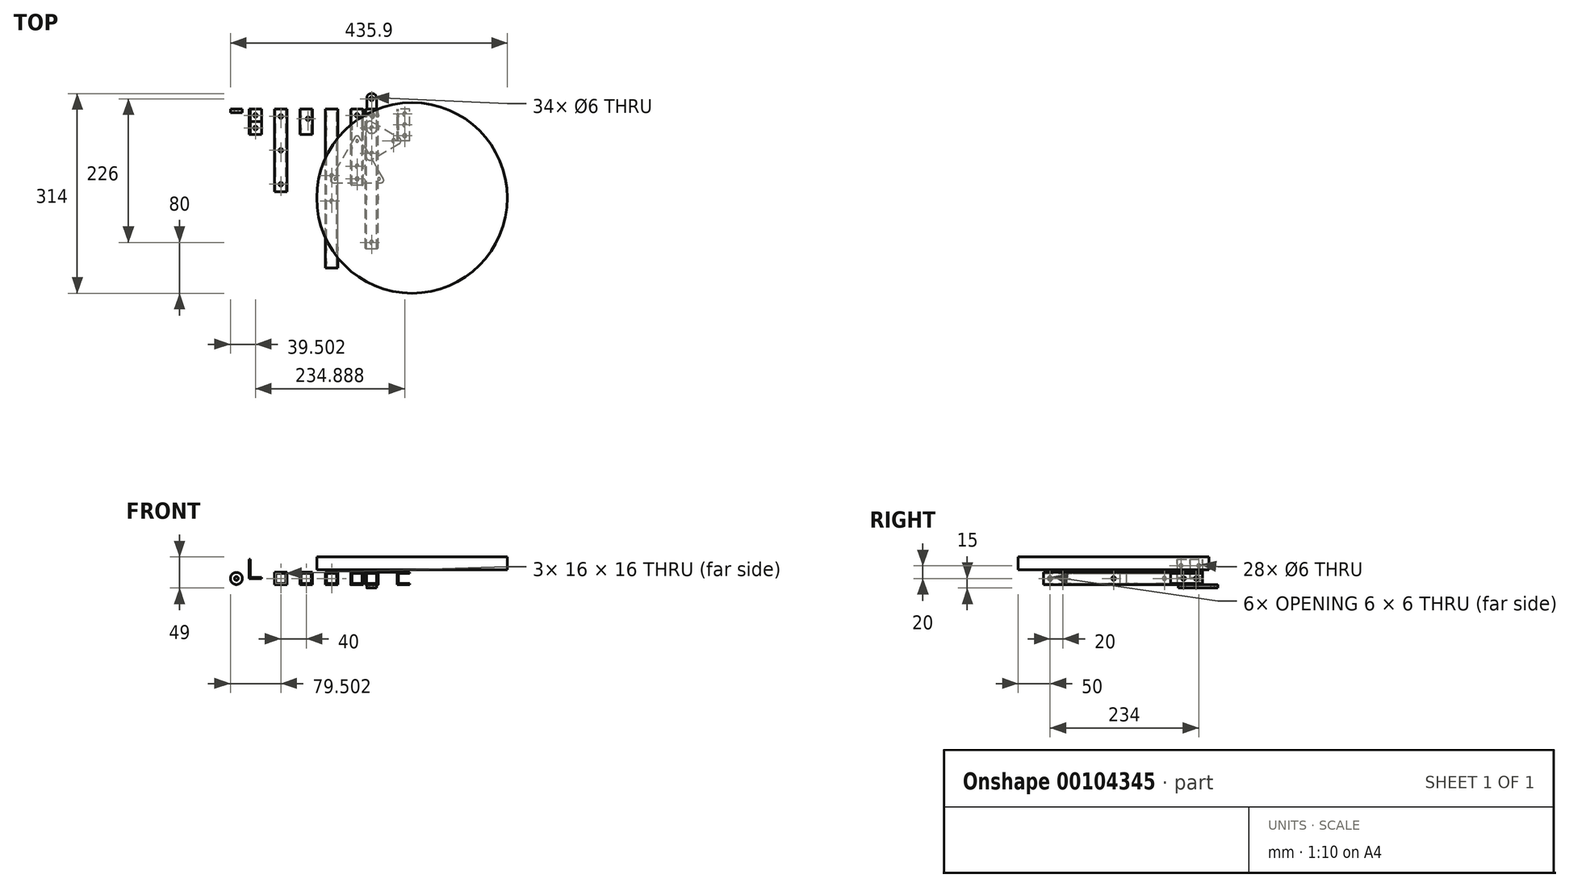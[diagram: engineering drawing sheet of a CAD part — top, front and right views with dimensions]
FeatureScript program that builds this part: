
annotation { "Feature Type Name" : "Feature", "Feature Type Description" : "" }
export const myFeature = defineFeature(function(context is Context, id is Id, definition is map)
    precondition{}
    {
        {
            var Q0;
            Q0=qCreatedBy(makeId("Front.planeOp"),FACE);
            var sketch = newSketch(context, id + "F0", { "sketchPlane" : qUnion([Q0])});
            skLineSegment(sketch, "E0.bottom", {"start": v(-10, 10) * mm, "end": v(10, 10) * mm});
            skLineSegment(sketch, "E0.top", {"start": v(-10, -10) * mm, "end": v(10, -10) * mm});
            skLineSegment(sketch, "E0.left", {"start": v(-10, 10) * mm, "end": v(-10, -10) * mm});
            skLineSegment(sketch, "E0.right", {"start": v(10, 10) * mm, "end": v(10, -10) * mm});
            skLineSegment(sketch, "E1.bottom", {"start": v(-8, 8) * mm, "end": v(8, 8) * mm});
            skLineSegment(sketch, "E1.top", {"start": v(-8, -8) * mm, "end": v(8, -8) * mm});
            skLineSegment(sketch, "E1.left", {"start": v(-8, 8) * mm, "end": v(-8, -8) * mm});
            skLineSegment(sketch, "E1.right", {"start": v(8, 8) * mm, "end": v(8, -8) * mm});
            skSolve(sketch);
        }
        {
            var Q0;
            Q0 = qSketchRegion(id + "F0", true);
            extrude(context, id + "F1", {"entities" : qUnion([Q0]), "offsetDistance" : 25 * mm, "depth" : 220 * mm});
        }
        {
            var Q0;
            Q0=makeQuery(id+"F1.opExtrude","SWEPT_FACE",FACE,{"disambiguationData":[OSD([sQuery(id+"F0.wireOp",EDGE,"E0.bottom")])]});
            var sketch = newSketch(context, id + "F2", { "sketchPlane" : qUnion([Q0])});
            skCircle(sketch, "E2", {"center": v(0, -30) * mm, "radius": 3 * mm});
            skCircle(sketch, "E3", {"center": v(0, -70) * mm, "radius": 3 * mm});
            skCircle(sketch, "E4", {"center": v(0, -210) * mm, "radius": 3 * mm});
            skSolve(sketch);
        }
        {
            var Q0;
            Q0 = qSketchRegion(id + "F2", true);
            var Q1;
            Q1=makeQuery(id+"F1.opExtrude","SWEPT_FACE",FACE,{"disambiguationData":[OSD([sQuery(id+"F0.wireOp",EDGE,"E0.top")])]});
            extrude(context, id + "F3", {"entities" : qUnion([Q0]), "operationType" : NewBodyOperationType.REMOVE, "endBound" : BoundingType.UP_TO_SURFACE, "oppositeDirection" : true, "endBoundEntityFace" : qUnion([Q1]), "offsetDistance" : 25 * mm, "depth" : 25 * mm});
        }
        {
            var Q0;
            Q0=makeQuery(id+"F1.opExtrude","SWEPT_FACE",FACE,{"disambiguationData":[OSD([sQuery(id+"F0.wireOp",EDGE,"E0.bottom")])]});
            var sketch = newSketch(context, id + "F4", { "sketchPlane" : qUnion([Q0])});
            skLineSegment(sketch, "E5", {"start": v(-8.66, -85) * mm, "end": v(-8.66, -15) * mm});
            skLineSegment(sketch, "E6", {"start": v(-8.66, -15) * mm, "end": v(51.96, -50) * mm});
            skLineSegment(sketch, "E7", {"start": v(51.96, -50) * mm, "end": v(-8.66, -85) * mm});
            skCircle(sketch, "E8", {"center": v(0, -30) * mm, "radius": 3 * mm});
            skLineSegment(sketch, "E9", {"start": v(-8.66, -50) * mm, "end": v(51.96, -50) * mm, "construction": true});
            skLineSegment(sketch, "E10", {"start": v(-8.66, -15) * mm, "end": v(21.65, -67.5) * mm, "construction": true});
            skCircle(sketch, "E11.1.0", {"center": v(0, -70) * mm, "radius": 3 * mm});
            skCircle(sketch, "E11.2.0", {"center": v(34.64, -50) * mm, "radius": 3 * mm});
            skPoint(sketch, "E11.center", {"position": v(11.55, -50) * mm});
            skSolve(sketch);
        }
        {
            var Q0;
            Q0 = qSketchRegion(id + "F4", true);
            extrude(context, id + "F5", {"entities" : qUnion([Q0]), "depth" : 2 * mm});
        }
        {
            var Q0;
            Q0=makeQuery(id+"F5.opExtrude","SWEPT_EDGE",EDGE,{"disambiguationData":[OSD([sQuery(id+"F4.wireOp",EDGE,"E5"),sQuery(id+"F4.wireOp",EDGE,"E7")])]});
            var Q1;
            Q1=makeQuery(id+"F5.opExtrude","SWEPT_EDGE",EDGE,{"disambiguationData":[OSD([sQuery(id+"F4.wireOp",EDGE,"E5"),sQuery(id+"F4.wireOp",EDGE,"E6")])]});
            var Q2;
            Q2=makeQuery(id+"F5.opExtrude","SWEPT_EDGE",EDGE,{"disambiguationData":[OSD([sQuery(id+"F4.wireOp",EDGE,"E6"),sQuery(id+"F4.wireOp",EDGE,"E7")])]});
            fillet(context, id + "F6", {"entities" : qUnion([Q0, Q1, Q2]), "radius" : 6 * mm, "tangentPropagation" : true, "allowEdgeOverflow" : false});
        }
        {
            var Q0;
            Q0=makeQuery(id+"F1.opExtrude","SWEPT_FACE",FACE,{"disambiguationData":[OSD([sQuery(id+"F0.wireOp",EDGE,"E0.top")])]});
            var sketch = newSketch(context, id + "F7", { "sketchPlane" : qUnion([Q0])});
            skCircle(sketch, "E12", {"center": v(0, 10) * mm, "radius": 3 * mm});
            skSolve(sketch);
        }
        {
            var Q0;
            Q0 = qSketchRegion(id + "F7", true);
            extrude(context, id + "F8", {"entities" : qUnion([Q0]), "operationType" : NewBodyOperationType.REMOVE, "endBound" : BoundingType.UP_TO_NEXT, "oppositeDirection" : true, "depth" : 25 * mm});
        }
        {
            var Q0;
            Q0=makeQuery(id+"F1.opExtrude","SWEPT_FACE",FACE,{"disambiguationData":[OSD([sQuery(id+"F0.wireOp",EDGE,"E0.bottom")])]});
            var sketch = newSketch(context, id + "F9", { "sketchPlane" : qUnion([Q0])});
            skCircle(sketch, "E13", {"center": v(0, -10) * mm, "radius": 5 * mm});
            skSolve(sketch);
        }
        {
            var Q0;
            Q0 = qSketchRegion(id + "F9", true);
            extrude(context, id + "F10", {"entities" : qUnion([Q0]), "operationType" : NewBodyOperationType.REMOVE, "endBound" : BoundingType.UP_TO_NEXT, "oppositeDirection" : true, "depth" : 25 * mm, "offsetDistance" : 25 * mm});
        }
        {
            var Q0;
            Q0=makeQuery(id+"F1.opExtrude","SWEPT_FACE",FACE,{"disambiguationData":[OSD([sQuery(id+"F0.wireOp",EDGE,"E0.top")])]});
            var sketch = newSketch(context, id + "F11", { "sketchPlane" : qUnion([Q0])});
            skLineSegment(sketch, "E14.bottom", {"start": v(7.5, 38) * mm, "end": v(-7.5, 38) * mm});
            skLineSegment(sketch, "E14.top", {"start": v(7.5, -24) * mm, "end": v(-7.5, -24) * mm});
            skLineSegment(sketch, "E14.left", {"start": v(7.5, 38) * mm, "end": v(7.5, -24) * mm});
            skLineSegment(sketch, "E14.right", {"start": v(-7.5, 38) * mm, "end": v(-7.5, -24) * mm});
            skCircle(sketch, "E15", {"center": v(0, 30) * mm, "radius": 3 * mm});
            skCircle(sketch, "E16", {"center": v(0, 10) * mm, "radius": 3 * mm});
            skCircle(sketch, "E17", {"center": v(0, -16) * mm, "radius": 3 * mm});
            skPoint(sketch, "E18", {"position": v(0, -24) * mm});
            skPoint(sketch, "E19", {"position": v(34.64, 50) * mm});
            skPoint(sketch, "E20", {"position": v(0, 210) * mm});
            skSolve(sketch);
        }
        {
            var Q0;
            Q0 = qSketchRegion(id + "F11", true);
            extrude(context, id + "F12", {"entities" : qUnion([Q0]), "depth" : 5 * mm});
        }
        {
            var Q0;
            Q0=qCreatedBy(makeId("Front.planeOp"),FACE);
            var sketch = newSketch(context, id + "F13", { "sketchPlane" : qUnion([Q0])});
            skLineSegment(sketch, "E21", {"start": v(60, 10) * mm, "end": v(40, 10) * mm});
            skLineSegment(sketch, "E22", {"start": v(40, 10) * mm, "end": v(40, -10) * mm});
            skLineSegment(sketch, "E23", {"start": v(40, -10) * mm, "end": v(60, -10) * mm});
            skLineSegment(sketch, "E24", {"start": v(60, -10) * mm, "end": v(60, -8) * mm});
            skLineSegment(sketch, "E25", {"start": v(60, -8) * mm, "end": v(42, -8) * mm});
            skLineSegment(sketch, "E26", {"start": v(42, -8) * mm, "end": v(42, 8) * mm});
            skLineSegment(sketch, "E27", {"start": v(42, 8) * mm, "end": v(60, 8) * mm});
            skLineSegment(sketch, "E28", {"start": v(60, 8) * mm, "end": v(60, 10) * mm});
            skLineSegment(sketch, "E29", {"start": v(42, 8) * mm, "end": v(40, 8) * mm, "construction": true});
            skSolve(sketch);
        }
        {
            var Q0;
            Q0 = qSketchRegion(id + "F13", true);
            extrude(context, id + "F14", {"entities" : qUnion([Q0]), "depth" : 50 * mm});
        }
        {
            var Q0;
            Q0=makeQuery(id+"F14.opExtrude","SWEPT_FACE",FACE,{"disambiguationData":[OSD([sQuery(id+"F13.wireOp",EDGE,"E23")])]});
            var sketch = newSketch(context, id + "F15", { "sketchPlane" : qUnion([Q0])});
            skCircle(sketch, "E30", {"center": v(52, 25) * mm, "radius": 3 * mm});
            skCircle(sketch, "E31", {"center": v(52, 8) * mm, "radius": 3 * mm});
            skSolve(sketch);
        }
        {
            var Q0;
            Q0 = qSketchRegion(id + "F15", true);
            extrude(context, id + "F16", {"entities" : qUnion([Q0]), "operationType" : NewBodyOperationType.REMOVE, "endBound" : BoundingType.UP_TO_NEXT, "oppositeDirection" : true, "depth" : 25 * mm});
        }
        {
            var Q0;
            Q0=makeQuery(id+"F14.opExtrude","SWEPT_FACE",FACE,{"disambiguationData":[OSD([sQuery(id+"F13.wireOp",EDGE,"E21")])]});
            var sketch = newSketch(context, id + "F17", { "sketchPlane" : qUnion([Q0])});
            skCircle(sketch, "E32", {"center": v(52, -42) * mm, "radius": 3 * mm});
            skPoint(sketch, "E33", {"position": v(52, -25) * mm});
            skSolve(sketch);
        }
        {
            var Q0;
            Q0 = qSketchRegion(id + "F17", true);
            var Q1;
            Q1=makeQuery(id+"F14.opExtrude","SWEPT_FACE",FACE,{"disambiguationData":[OSD([sQuery(id+"F13.wireOp",EDGE,"E23")])]});
            extrude(context, id + "F18", {"entities" : qUnion([Q0]), "operationType" : NewBodyOperationType.REMOVE, "endBound" : BoundingType.UP_TO_SURFACE, "oppositeDirection" : true, "endBoundEntityFace" : qUnion([Q1]), "offsetDistance" : 25 * mm, "depth" : 25 * mm});
        }
        {
            var Q0;
            Q0=makeQuery(id+"F12.opExtrude","SWEPT_EDGE",EDGE,{"disambiguationData":[OSD([sQuery(id+"F11.wireOp",EDGE,"E14.bottom"),sQuery(id+"F11.wireOp",EDGE,"E14.left")])]});
            var Q1;
            Q1=makeQuery(id+"F12.opExtrude","SWEPT_EDGE",EDGE,{"disambiguationData":[OSD([sQuery(id+"F11.wireOp",EDGE,"E14.bottom"),sQuery(id+"F11.wireOp",EDGE,"E14.right")])]});
            var Q2;
            Q2=makeQuery(id+"F12.opExtrude","SWEPT_EDGE",EDGE,{"disambiguationData":[OSD([sQuery(id+"F11.wireOp",EDGE,"E14.top"),sQuery(id+"F11.wireOp",EDGE,"E14.right")])]});
            var Q3;
            Q3=makeQuery(id+"F12.opExtrude","SWEPT_EDGE",EDGE,{"disambiguationData":[OSD([sQuery(id+"F11.wireOp",EDGE,"E14.top"),sQuery(id+"F11.wireOp",EDGE,"E14.left")])]});
            fillet(context, id + "F19", {"entities" : qUnion([Q0, Q1, Q2, Q3]), "radius" : 6 * mm, "tangentPropagation" : true, "allowEdgeOverflow" : false});
        }
        {
            var Q0;
            Q0=makeQuery(id+"F1.opExtrude","CAP_EDGE",EDGE,{"disambiguationData":[OSD([sQuery(id+"F0.wireOp",EDGE,"E0.right")])],"isStart":false});
            var Q1;
            Q1=makeQuery(id+"F1.opExtrude","CAP_EDGE",EDGE,{"disambiguationData":[OSD([sQuery(id+"F0.wireOp",EDGE,"E0.left")])],"isStart":false});
            var Q2;
            Q2=makeQuery(id+"F1.opExtrude","CAP_EDGE",EDGE,{"disambiguationData":[OSD([sQuery(id+"F0.wireOp",EDGE,"E0.right")])],"isStart":true});
            var Q3;
            Q3=makeQuery(id+"F1.opExtrude","CAP_EDGE",EDGE,{"disambiguationData":[OSD([sQuery(id+"F0.wireOp",EDGE,"E0.left")])],"isStart":true});
            fillet(context, id + "F20", {"entities" : qUnion([Q0, Q1, Q2, Q3]), "radius" : 2 * mm, "tangentPropagation" : true, "allowEdgeOverflow" : false});
        }
        {
            var Q0;
            Q0=makeQuery(id+"F1.opExtrude","SWEPT_FACE",FACE,{"disambiguationData":[OSD([sQuery(id+"F0.wireOp",EDGE,"E0.right")])]});
            var sketch = newSketch(context, id + "F21", { "sketchPlane" : qUnion([Q0])});
            skCircle(sketch, "E34", {"center": v(-140, 0) * mm, "radius": 3 * mm});
            skPoint(sketch, "E35", {"position": v(-210, 0) * mm});
            skPoint(sketch, "E36", {"position": v(-30, 0) * mm});
            skLineSegment(sketch, "E37", {"start": v(-140, 10) * mm, "end": v(-140, -10) * mm, "construction": true});
            skPoint(sketch, "E38", {"position": v(-250, 0) * mm});
            skSolve(sketch);
        }
        {
            var Q0;
            Q0 = qSketchRegion(id + "F21", true);
            var Q1;
            Q1=makeQuery(id+"F1.opExtrude","SWEPT_FACE",FACE,{"disambiguationData":[OSD([sQuery(id+"F0.wireOp",EDGE,"E0.left")])]});
            extrude(context, id + "F22", {"entities" : qUnion([Q0]), "operationType" : NewBodyOperationType.REMOVE, "endBound" : BoundingType.UP_TO_SURFACE, "oppositeDirection" : true, "endBoundEntityFace" : qUnion([Q1]), "depth" : 25 * mm});
        }
        {
            var Q0;
            Q0=makeQuery(id+"F5.opExtrude","CAP_FACE",FACE,{"disambiguationData":[OSD([sQuery(id+"F4.wireOp",EDGE,"E5"),sQuery(id+"F4.wireOp",EDGE,"E6"),sQuery(id+"F4.wireOp",EDGE,"E7"),sQuery(id+"F4.wireOp",EDGE,"E8"),sQuery(id+"F4.wireOp",EDGE,"E11.1.0"),sQuery(id+"F4.wireOp",EDGE,"E11.2.0")])],"isStart":false});
            var sketch = newSketch(context, id + "F23", { "sketchPlane" : qUnion([Q0])});
            skCircle(sketch, "E39", {"center": v(63.5, -140) * mm, "radius": 60 * mm, "construction": true});
            skCircle(sketch, "E40", {"center": v(63.5, -140) * mm, "radius": 124.5 * mm, "construction": true});
            skLineSegment(sketch, "E41", {"start": v(-60.79, -116) * mm, "end": v(15.01, -116) * mm});
            skLineSegment(sketch, "E42", {"start": v(18.48, -110) * mm, "end": v(-19.42, -44.36) * mm});
            skLineSegment(sketch, "E43", {"start": v(-26.35, -44.36) * mm, "end": v(-64.25, -110) * mm});
            skCircle(sketch, "E44", {"center": v(-22.89, -50.36) * mm, "radius": 2 * mm});
            skCircle(sketch, "E45", {"center": v(11.55, -110) * mm, "radius": 2 * mm});
            skCircle(sketch, "E46", {"center": v(-57.32, -110) * mm, "radius": 2 * mm});
            skLineSegment(sketch, "E47", {"start": v(-22.89, -50.36) * mm, "end": v(-22.89, -38.36) * mm, "construction": true});
            skLineSegment(sketch, "E48", {"start": v(-57.32, -110) * mm, "end": v(-67.72, -116) * mm, "construction": true});
            skLineSegment(sketch, "E49", {"start": v(11.55, -110) * mm, "end": v(21.94, -116) * mm, "construction": true});
            skPoint(sketch, "E50.visualSharp", {"position": v(-67.72, -116) * mm});
            skArc(sketch, "E50.filletArc", {"start": v(-64.25, -110) * mm, "mid": v(-64.25, -114) * mm, "end": v(-60.79, -116) * mm});
            skPoint(sketch, "E51.visualSharp", {"position": v(21.94, -116) * mm});
            skArc(sketch, "E51.filletArc", {"start": v(15.01, -116) * mm, "mid": v(18.48, -114) * mm, "end": v(18.48, -110) * mm});
            skPoint(sketch, "E52.visualSharp", {"position": v(-22.89, -38.36) * mm});
            skArc(sketch, "E52.filletArc", {"start": v(-19.42, -44.36) * mm, "mid": v(-22.89, -42.36) * mm, "end": v(-26.35, -44.36) * mm});
            skLineSegment(sketch, "E53", {"start": v(63.5, -140) * mm, "end": v(0, -30) * mm, "construction": true});
            skLineSegment(sketch, "E54", {"start": v(63.5, -140) * mm, "end": v(0, -250) * mm, "construction": true});
            skLineSegment(sketch, "E55", {"start": v(-67.72, -116) * mm, "end": v(-0.47, -77.18) * mm, "construction": true});
            skCircle(sketch, "E56", {"center": v(-22.89, -90.12) * mm, "radius": 3 * mm});
            skLineSegment(sketch, "E57", {"start": v(0, -210) * mm, "end": v(0, -250) * mm, "construction": true});
            skCircle(sketch, "E58", {"center": v(63.5, -140) * mm, "radius": 150 * mm, "construction": true});
            skLineSegment(sketch, "E59", {"start": v(34.64, -230) * mm, "end": v(0, -250) * mm, "construction": true});
            skLineSegment(sketch, "E60", {"start": v(63.5, -140) * mm, "end": v(-86.18, -180.11) * mm, "construction": true});
            skLineSegment(sketch, "E61", {"start": v(-77.58, -165.2) * mm, "end": v(112.22, -274.8) * mm, "construction": true});
            skLineSegment(sketch, "E62", {"start": v(-77.58, -165.2) * mm, "end": v(-86.18, -180.11) * mm, "construction": true});
            skLineSegment(sketch, "E63", {"start": v(63.5, -140) * mm, "end": v(-69.57, -242.11) * mm, "construction": true});
            skLineSegment(sketch, "E64", {"start": v(63.5, -140) * mm, "end": v(-102.8, -118.1) * mm, "construction": true});
            skLineSegment(sketch, "E65", {"start": v(-102.8, -118.1) * mm, "end": v(-69.57, -242.11) * mm, "construction": true});
            skLineSegment(sketch, "E66.bottom", {"start": v(130.57, -273.84) * mm, "end": v(-85.93, -148.84) * mm, "construction": true});
            skLineSegment(sketch, "E66.top", {"start": v(120.57, -291.16) * mm, "end": v(-95.93, -166.16) * mm, "construction": true});
            skLineSegment(sketch, "E66.left", {"start": v(130.57, -273.84) * mm, "end": v(120.57, -291.16) * mm, "construction": true});
            skLineSegment(sketch, "E66.right", {"start": v(-85.93, -148.84) * mm, "end": v(-95.93, -166.16) * mm, "construction": true});
            skPoint(sketch, "E66.middle", {"position": v(17.32, -220) * mm});
            skLineSegment(sketch, "E67.bottom", {"start": v(-88.78, -119.95) * mm, "end": v(-108.6, -117.34) * mm, "construction": true});
            skLineSegment(sketch, "E67.top", {"start": v(-91.39, -139.78) * mm, "end": v(-111.22, -137.17) * mm, "construction": true});
            skLineSegment(sketch, "E67.left", {"start": v(-88.78, -119.95) * mm, "end": v(-91.39, -139.78) * mm, "construction": true});
            skLineSegment(sketch, "E67.right", {"start": v(-108.6, -117.34) * mm, "end": v(-111.22, -137.17) * mm, "construction": true});
            skPoint(sketch, "E67.middle", {"position": v(-100, -128.56) * mm});
            skPoint(sketch, "E68", {"position": v(-94.73, -119.17) * mm});
            skPoint(sketch, "E69", {"position": v(-72.37, -231.66) * mm});
            skSolve(sketch);
        }
        {
            var Q0;
            Q0 = qSketchRegion(id + "F23", true);
            extrude(context, id + "F24", {"entities" : qUnion([Q0]), "depth" : 2 * mm});
        }
        {
            var Q0;
            Q0=qCreatedBy(makeId("Front.planeOp"),FACE);
            var sketch = newSketch(context, id + "F25", { "sketchPlane" : qUnion([Q0])});
            skLineSegment(sketch, "E70.bottom", {"start": v(-14.89, 8) * mm, "end": v(-30.89, 8) * mm});
            skLineSegment(sketch, "E70.top", {"start": v(-14.89, -8) * mm, "end": v(-30.89, -8) * mm});
            skLineSegment(sketch, "E70.left", {"start": v(-14.89, 8) * mm, "end": v(-14.89, -8) * mm});
            skLineSegment(sketch, "E70.right", {"start": v(-30.89, 8) * mm, "end": v(-30.89, -8) * mm});
            skPoint(sketch, "E70.middle", {"position": v(-22.89, 0) * mm});
            skLineSegment(sketch, "E71.bottom", {"start": v(-12.89, 10) * mm, "end": v(-32.89, 10) * mm});
            skLineSegment(sketch, "E71.top", {"start": v(-12.89, -10) * mm, "end": v(-32.89, -10) * mm});
            skLineSegment(sketch, "E71.left", {"start": v(-12.89, 10) * mm, "end": v(-12.89, -10) * mm});
            skLineSegment(sketch, "E71.right", {"start": v(-32.89, 10) * mm, "end": v(-32.89, -10) * mm});
            skLineSegment(sketch, "E72", {"start": v(-22.89, 0) * mm, "end": v(-22.89, 0) * mm});
            skSolve(sketch);
        }
        {
            var Q0;
            Q0 = qSketchRegion(id + "F25", true);
            extrude(context, id + "F26", {"entities" : qUnion([Q0]), "depth" : 120 * mm});
        }
        {
            var Q0;
            Q0=makeQuery(id+"F26.opExtrude","SWEPT_FACE",FACE,{"disambiguationData":[OSD([sQuery(id+"F25.wireOp",EDGE,"E71.bottom")])]});
            var sketch = newSketch(context, id + "F27", { "sketchPlane" : qUnion([Q0])});
            skCircle(sketch, "E73", {"center": v(-22.89, -10) * mm, "radius": 3 * mm});
            skCircle(sketch, "E74", {"center": v(-22.89, -110) * mm, "radius": 3 * mm});
            skPoint(sketch, "E75", {"position": v(-22.89, 0) * mm});
            skLineSegment(sketch, "E76", {"start": v(-22.89, -110) * mm, "end": v(-22.89, -120) * mm, "construction": true});
            skLineSegment(sketch, "E77", {"start": v(-22.89, -10) * mm, "end": v(-22.89, 0) * mm, "construction": true});
            skSolve(sketch);
        }
        {
            var Q0;
            Q0 = qSketchRegion(id + "F27", true);
            extrude(context, id + "F28", {"entities" : qUnion([Q0]), "operationType" : NewBodyOperationType.REMOVE, "endBound" : BoundingType.UP_TO_NEXT, "oppositeDirection" : true, "depth" : 25 * mm});
        }
        {
            var Q0;
            Q0=makeQuery(id+"F26.opExtrude","SWEPT_FACE",FACE,{"disambiguationData":[OSD([sQuery(id+"F25.wireOp",EDGE,"E71.right")])]});
            var sketch = newSketch(context, id + "F29", { "sketchPlane" : qUnion([Q0])});
            skCircle(sketch, "E78", {"center": v(60, 0) * mm, "radius": 3 * mm});
            skLineSegment(sketch, "E79", {"start": v(60, -10) * mm, "end": v(60, 0) * mm});
            skSolve(sketch);
        }
        {
            var Q0;
            Q0 = qSketchRegion(id + "F29", true);
            var Q1;
            Q1=makeQuery(id+"F26.opExtrude","SWEPT_FACE",FACE,{"disambiguationData":[OSD([sQuery(id+"F25.wireOp",EDGE,"E71.left")])]});
            extrude(context, id + "F30", {"entities" : qUnion([Q0]), "operationType" : NewBodyOperationType.REMOVE, "endBound" : BoundingType.UP_TO_SURFACE, "oppositeDirection" : true, "endBoundEntityFace" : qUnion([Q1]), "depth" : 25 * mm});
        }
        {
            var Q0;
            Q0=makeQuery(id+"F26.opExtrude","CAP_EDGE",EDGE,{"disambiguationData":[OSD([sQuery(id+"F25.wireOp",EDGE,"E71.right")])],"isStart":false});
            var Q1;
            Q1=makeQuery(id+"F26.opExtrude","CAP_EDGE",EDGE,{"disambiguationData":[OSD([sQuery(id+"F25.wireOp",EDGE,"E71.left")])],"isStart":false});
            var Q2;
            Q2=makeQuery(id+"F26.opExtrude","CAP_EDGE",EDGE,{"disambiguationData":[OSD([sQuery(id+"F25.wireOp",EDGE,"E71.right")])],"isStart":true});
            var Q3;
            Q3=makeQuery(id+"F26.opExtrude","CAP_EDGE",EDGE,{"disambiguationData":[OSD([sQuery(id+"F25.wireOp",EDGE,"E71.left")])],"isStart":true});
            fillet(context, id + "F31", {"entities" : qUnion([Q0, Q1, Q2, Q3]), "radius" : 2 * mm, "tangentPropagation" : true, "allowEdgeOverflow" : false});
        }
        {
            var Q0;
            Q0=makeQuery(id+"F24.opExtrude","CAP_FACE",FACE,{"disambiguationData":[OSD([sQuery(id+"F23.wireOp",EDGE,"E41"),sQuery(id+"F23.wireOp",EDGE,"E42"),sQuery(id+"F23.wireOp",EDGE,"E43"),sQuery(id+"F23.wireOp",EDGE,"E44"),sQuery(id+"F23.wireOp",EDGE,"E45"),sQuery(id+"F23.wireOp",EDGE,"E46"),sQuery(id+"F23.wireOp",EDGE,"E50.filletArc"),sQuery(id+"F23.wireOp",EDGE,"E51.filletArc"),sQuery(id+"F23.wireOp",EDGE,"E52.filletArc"),sQuery(id+"F23.wireOp",EDGE,"E56")])],"isStart":false});
            var sketch = newSketch(context, id + "F32", { "sketchPlane" : qUnion([Q0])});
            skCircle(sketch, "E80", {"center": v(63.5, -140) * mm, "radius": 150 * mm});
            skSolve(sketch);
        }
        {
            var Q0;
            Q0 = qSketchRegion(id + "F32", true);
            extrude(context, id + "F33", {"entities" : qUnion([Q0]), "depth" : 20 * mm});
        }
        {
            var Q0;
            Q0=qCreatedBy(makeId("Front.planeOp"),FACE);
            var sketch = newSketch(context, id + "F34", { "sketchPlane" : qUnion([Q0])});
            skLineSegment(sketch, "E81.bottom", {"start": v(-72.89, -10) * mm, "end": v(-52.89, -10) * mm});
            skLineSegment(sketch, "E81.top", {"start": v(-72.89, 10) * mm, "end": v(-52.89, 10) * mm});
            skLineSegment(sketch, "E81.left", {"start": v(-72.89, -10) * mm, "end": v(-72.89, 10) * mm});
            skLineSegment(sketch, "E81.right", {"start": v(-52.89, -10) * mm, "end": v(-52.89, 10) * mm});
            skLineSegment(sketch, "E82.bottom", {"start": v(-70.89, 8) * mm, "end": v(-54.89, 8) * mm});
            skLineSegment(sketch, "E82.top", {"start": v(-70.89, -8) * mm, "end": v(-54.89, -8) * mm});
            skLineSegment(sketch, "E82.left", {"start": v(-70.89, 8) * mm, "end": v(-70.89, -8) * mm});
            skLineSegment(sketch, "E82.right", {"start": v(-54.89, 8) * mm, "end": v(-54.89, -8) * mm});
            skSolve(sketch);
        }
        {
            var Q0;
            Q0 = qSketchRegion(id + "F34", true);
            extrude(context, id + "F35", {"entities" : qUnion([Q0]), "depth" : 250 * mm, "offsetDistance" : 25 * mm});
        }
        {
            var Q0;
            Q0=makeQuery(id+"F35.opExtrude","SWEPT_FACE",FACE,{"disambiguationData":[OSD([sQuery(id+"F34.wireOp",EDGE,"E81.top")])]});
            var sketch = newSketch(context, id + "F36", { "sketchPlane" : qUnion([Q0])});
            skCircle(sketch, "E83", {"center": v(-62.89, -105) * mm, "radius": 3 * mm});
            skCircle(sketch, "E84", {"center": v(-62.89, -145) * mm, "radius": 3 * mm});
            skLineSegment(sketch, "E85", {"start": v(-72.89, -125) * mm, "end": v(-52.89, -125) * mm, "construction": true});
            skPoint(sketch, "E86", {"position": v(-62.89, -125) * mm});
            skSolve(sketch);
        }
        {
            var Q0;
            Q0 = qSketchRegion(id + "F36", true);
            extrude(context, id + "F37", {"entities" : qUnion([Q0]), "operationType" : NewBodyOperationType.REMOVE, "endBound" : BoundingType.THROUGH_ALL, "oppositeDirection" : true, "depth" : 25 * mm, "offsetDistance" : 25 * mm});
        }
        {
            var Q0;
            Q0=makeQuery(id+"F35.opExtrude","SWEPT_FACE",FACE,{"disambiguationData":[OSD([sQuery(id+"F34.wireOp",EDGE,"E81.left")])]});
            var sketch = newSketch(context, id + "F38", { "sketchPlane" : qUnion([Q0])});
            skCircle(sketch, "E87", {"center": v(10, 0) * mm, "radius": 3 * mm});
            skCircle(sketch, "E88", {"center": v(30, 0) * mm, "radius": 3 * mm});
            skCircle(sketch, "E89", {"center": v(220, 0) * mm, "radius": 3 * mm});
            skCircle(sketch, "E90", {"center": v(240, 0) * mm, "radius": 3 * mm});
            skSolve(sketch);
        }
        {
            var Q0;
            Q0 = qSketchRegion(id + "F38", true);
            extrude(context, id + "F39", {"entities" : qUnion([Q0]), "operationType" : NewBodyOperationType.REMOVE, "endBound" : BoundingType.THROUGH_ALL, "oppositeDirection" : true, "depth" : 25 * mm, "offsetDistance" : 25 * mm});
        }
        {
            var Q0;
            Q0=qCreatedBy(makeId("Front.planeOp"),FACE);
            var sketch = newSketch(context, id + "F40", { "sketchPlane" : qUnion([Q0])});
            skLineSegment(sketch, "E91.bottom", {"start": v(-112.89, 10) * mm, "end": v(-92.89, 10) * mm});
            skLineSegment(sketch, "E91.top", {"start": v(-112.89, -10) * mm, "end": v(-92.89, -10) * mm});
            skLineSegment(sketch, "E91.left", {"start": v(-112.89, 10) * mm, "end": v(-112.89, -10) * mm});
            skLineSegment(sketch, "E91.right", {"start": v(-92.89, 10) * mm, "end": v(-92.89, -10) * mm});
            skLineSegment(sketch, "E92.bottom", {"start": v(-110.89, 8) * mm, "end": v(-94.89, 8) * mm});
            skLineSegment(sketch, "E92.top", {"start": v(-110.89, -8) * mm, "end": v(-94.89, -8) * mm});
            skLineSegment(sketch, "E92.left", {"start": v(-110.89, 8) * mm, "end": v(-110.89, -8) * mm});
            skLineSegment(sketch, "E92.right", {"start": v(-94.89, 8) * mm, "end": v(-94.89, -8) * mm});
            skSolve(sketch);
        }
        {
            var Q0;
            Q0 = qSketchRegion(id + "F40", true);
            extrude(context, id + "F41", {"entities" : qUnion([Q0]), "depth" : 40 * mm, "offsetDistance" : 25 * mm});
        }
        {
            var Q0;
            Q0=makeQuery(id+"F41.opExtrude","SWEPT_FACE",FACE,{"disambiguationData":[OSD([sQuery(id+"F40.wireOp",EDGE,"E91.left")])]});
            var sketch = newSketch(context, id + "F42", { "sketchPlane" : qUnion([Q0])});
            skCircle(sketch, "E93", {"center": v(10, 0) * mm, "radius": 3 * mm});
            skCircle(sketch, "E94", {"center": v(30, 0) * mm, "radius": 3 * mm});
            skSolve(sketch);
        }
        {
            var Q0;
            Q0 = qSketchRegion(id + "F42", true);
            extrude(context, id + "F43", {"entities" : qUnion([Q0]), "operationType" : NewBodyOperationType.REMOVE, "endBound" : BoundingType.THROUGH_ALL, "oppositeDirection" : true, "depth" : 25 * mm, "offsetDistance" : 25 * mm});
        }
        {
            var Q0;
            Q0=qCreatedBy(makeId("Front.planeOp"),FACE);
            var sketch = newSketch(context, id + "F44", { "sketchPlane" : qUnion([Q0])});
            skLineSegment(sketch, "E95.bottom", {"start": v(-132.89, 10) * mm, "end": v(-152.89, 10) * mm});
            skLineSegment(sketch, "E95.top", {"start": v(-132.89, -10) * mm, "end": v(-152.89, -10) * mm});
            skLineSegment(sketch, "E95.left", {"start": v(-132.89, 10) * mm, "end": v(-132.89, -10) * mm});
            skLineSegment(sketch, "E95.right", {"start": v(-152.89, 10) * mm, "end": v(-152.89, -10) * mm});
            skPoint(sketch, "E95.middle", {"position": v(-142.89, 0) * mm});
            skLineSegment(sketch, "E96.bottom", {"start": v(-134.89, 8) * mm, "end": v(-150.89, 8) * mm});
            skLineSegment(sketch, "E96.top", {"start": v(-134.89, -8) * mm, "end": v(-150.89, -8) * mm});
            skLineSegment(sketch, "E96.left", {"start": v(-134.89, 8) * mm, "end": v(-134.89, -8) * mm});
            skLineSegment(sketch, "E96.right", {"start": v(-150.89, 8) * mm, "end": v(-150.89, -8) * mm});
            skSolve(sketch);
        }
        {
            var Q0;
            Q0 = qSketchRegion(id + "F44", true);
            extrude(context, id + "F45", {"entities" : qUnion([Q0]), "depth" : 130 * mm, "offsetDistance" : 25 * mm});
        }
        {
            var Q0;
            Q0=makeQuery(id+"F45.opExtrude","SWEPT_FACE",FACE,{"disambiguationData":[OSD([sQuery(id+"F44.wireOp",EDGE,"E95.bottom")])]});
            var sketch = newSketch(context, id + "F46", { "sketchPlane" : qUnion([Q0])});
            skCircle(sketch, "E97", {"center": v(-142.89, -65) * mm, "radius": 3 * mm});
            skPoint(sketch, "E97.centerSnap0", {"position": v(-142.89, 0) * mm});
            skLineSegment(sketch, "E98", {"start": v(-152.89, -65) * mm, "end": v(-132.89, -65) * mm, "construction": true});
            skCircle(sketch, "E99", {"center": v(-142.89, -11.63) * mm, "radius": 3 * mm});
            skCircle(sketch, "E100", {"center": v(-142.89, -118.37) * mm, "radius": 3 * mm});
            skSolve(sketch);
        }
        {
            var Q0;
            Q0 = qSketchRegion(id + "F46", true);
            extrude(context, id + "F47", {"entities" : qUnion([Q0]), "operationType" : NewBodyOperationType.REMOVE, "endBound" : BoundingType.THROUGH_ALL, "oppositeDirection" : true, "depth" : 25 * mm, "offsetDistance" : 25 * mm});
        }
        {
            var Q0;
            Q0=makeQuery(id+"F41.opExtrude","SWEPT_FACE",FACE,{"disambiguationData":[OSD([sQuery(id+"F40.wireOp",EDGE,"E91.bottom")])]});
            var sketch = newSketch(context, id + "F48", { "sketchPlane" : qUnion([Q0])});
            skCircle(sketch, "E101", {"center": v(-100.1, -15.42) * mm, "radius": 3 * mm});
            skSolve(sketch);
        }
        {
            var Q0;
            Q0 = qSketchRegion(id + "F48", true);
            extrude(context, id + "F49", {"entities" : qUnion([Q0]), "operationType" : NewBodyOperationType.REMOVE, "endBound" : BoundingType.THROUGH_ALL, "oppositeDirection" : true, "depth" : 25 * mm, "offsetDistance" : 25 * mm});
        }
        {
            var Q0;
            Q0=qCreatedBy(makeId("Front.planeOp"),FACE);
            var sketch = newSketch(context, id + "F50", { "sketchPlane" : qUnion([Q0])});
            skLineSegment(sketch, "E102", {"start": v(-172.89, 0) * mm, "end": v(-192.89, 0) * mm});
            skLineSegment(sketch, "E103", {"start": v(-192.89, 0) * mm, "end": v(-192.89, 30) * mm});
            skLineSegment(sketch, "E104", {"start": v(-192.89, 30) * mm, "end": v(-190.89, 30) * mm});
            skLineSegment(sketch, "E105", {"start": v(-190.89, 30) * mm, "end": v(-190.89, 2) * mm});
            skLineSegment(sketch, "E106", {"start": v(-190.89, 2) * mm, "end": v(-172.89, 2) * mm});
            skLineSegment(sketch, "E107", {"start": v(-172.89, 2) * mm, "end": v(-172.89, 0) * mm});
            skSolve(sketch);
        }
        {
            var Q0;
            Q0 = qSketchRegion(id + "F50", true);
            extrude(context, id + "F51", {"entities" : qUnion([Q0]), "depth" : 20 * mm, "offsetDistance" : 25 * mm});
        }
        {
            var Q0;
            Q0=makeQuery(id+"F51.opExtrude","SWEPT_FACE",FACE,{"disambiguationData":[OSD([sQuery(id+"F50.wireOp",EDGE,"E102")])]});
            var sketch = newSketch(context, id + "F52", { "sketchPlane" : qUnion([Q0])});
            skCircle(sketch, "E108", {"center": v(-182.89, 10) * mm, "radius": 3 * mm});
            skPoint(sketch, "E108.centerSnap0", {"position": v(-172.89, 10) * mm});
            skPoint(sketch, "E108.centerSnap1", {"position": v(-182.89, 20) * mm});
            skSolve(sketch);
        }
        {
            var Q0;
            Q0 = qSketchRegion(id + "F52", true);
            extrude(context, id + "F53", {"entities" : qUnion([Q0]), "operationType" : NewBodyOperationType.REMOVE, "endBound" : BoundingType.UP_TO_NEXT, "oppositeDirection" : true, "depth" : 25 * mm, "offsetDistance" : 25 * mm});
        }
        {
            var Q0;
            Q0=makeQuery(id+"F51.opExtrude","SWEPT_FACE",FACE,{"disambiguationData":[OSD([sQuery(id+"F50.wireOp",EDGE,"E103")])]});
            var sketch = newSketch(context, id + "F54", { "sketchPlane" : qUnion([Q0])});
            skCircle(sketch, "E109", {"center": v(6, 20) * mm, "radius": 3 * mm});
            skSolve(sketch);
        }
        {
            var Q0;
            Q0 = qSketchRegion(id + "F54", true);
            extrude(context, id + "F55", {"entities" : qUnion([Q0]), "operationType" : NewBodyOperationType.REMOVE, "endBound" : BoundingType.UP_TO_NEXT, "oppositeDirection" : true, "depth" : 25 * mm, "offsetDistance" : 25 * mm});
        }
        {
            var Q0;
            Q0=qCreatedBy(makeId("Front.planeOp"),FACE);
            var sketch = newSketch(context, id + "F56", { "sketchPlane" : qUnion([Q0])});
            skCircle(sketch, "E110", {"center": v(-212.89, 0) * mm, "radius": 9.5 * mm});
            skCircle(sketch, "E111", {"center": v(-212.89, 0) * mm, "radius": 3 * mm});
            skSolve(sketch);
        }
        {
            var Q0;
            Q0 = qSketchRegion(id + "F56", true);
            extrude(context, id + "F57", {"entities" : qUnion([Q0]), "depth" : 6 * mm, "offsetDistance" : 25 * mm});
        }
        {
            var Q0;
            Q0=makeQuery(id+"F51.opExtrude","CAP_FACE",FACE,{"disambiguationData":[OSD([sQuery(id+"F50.wireOp",EDGE,"E102"),sQuery(id+"F50.wireOp",EDGE,"E103"),sQuery(id+"F50.wireOp",EDGE,"E104"),sQuery(id+"F50.wireOp",EDGE,"E105"),sQuery(id+"F50.wireOp",EDGE,"E106"),sQuery(id+"F50.wireOp",EDGE,"E107")])],"isStart":false});
            var sketch = newSketch(context, id + "F58", { "sketchPlane" : qUnion([Q0])});
            skLineSegment(sketch, "E112", {"start": v(-192.89, 30) * mm, "end": v(-192.89, 0) * mm});
            skLineSegment(sketch, "E113", {"start": v(-192.89, 0) * mm, "end": v(-172.89, 0) * mm});
            skLineSegment(sketch, "E114", {"start": v(-172.89, 0) * mm, "end": v(-172.89, 2) * mm});
            skLineSegment(sketch, "E115", {"start": v(-172.89, 2) * mm, "end": v(-190.89, 2) * mm});
            skLineSegment(sketch, "E116", {"start": v(-190.89, 2) * mm, "end": v(-190.89, 30) * mm});
            skLineSegment(sketch, "E117", {"start": v(-190.89, 30) * mm, "end": v(-192.89, 30) * mm});
            skSolve(sketch);
        }
        {
            var Q0;
            Q0 = qSketchRegion(id + "F58", true);
            extrude(context, id + "F59", {"entities" : qUnion([Q0]), "depth" : 20 * mm, "offsetDistance" : 25 * mm});
        }
        {
            var Q0;
            Q0=makeQuery(id+"F59.opExtrude","SWEPT_FACE",FACE,{"disambiguationData":[OSD([sQuery(id+"F58.wireOp",EDGE,"E113")])]});
            var sketch = newSketch(context, id + "F60", { "sketchPlane" : qUnion([Q0])});
            skCircle(sketch, "E118", {"center": v(-182.89, 30) * mm, "radius": 3 * mm});
            skPoint(sketch, "E118.centerSnap0", {"position": v(-172.89, 30) * mm});
            skPoint(sketch, "E118.centerSnap1", {"position": v(-182.89, 40) * mm});
            skSolve(sketch);
        }
        {
            var Q0;
            Q0 = qSketchRegion(id + "F60", true);
            extrude(context, id + "F61", {"entities" : qUnion([Q0]), "operationType" : NewBodyOperationType.REMOVE, "endBound" : BoundingType.UP_TO_NEXT, "oppositeDirection" : true, "depth" : 25 * mm, "offsetDistance" : 25 * mm});
        }
        {
            var Q0;
            Q0=makeQuery(id+"F59.opExtrude","SWEPT_FACE",FACE,{"disambiguationData":[OSD([sQuery(id+"F58.wireOp",EDGE,"E112")])]});
            var sketch = newSketch(context, id + "F62", { "sketchPlane" : qUnion([Q0])});
            skCircle(sketch, "E119", {"center": v(34, 20) * mm, "radius": 3 * mm});
            skPoint(sketch, "E120", {"position": v(6, 20) * mm});
            skSolve(sketch);
        }
        {
            var Q0;
            Q0 = qSketchRegion(id + "F62", true);
            extrude(context, id + "F63", {"entities" : qUnion([Q0]), "operationType" : NewBodyOperationType.REMOVE, "endBound" : BoundingType.UP_TO_NEXT, "oppositeDirection" : true, "depth" : 25 * mm, "offsetDistance" : 25 * mm});
        }
    });
